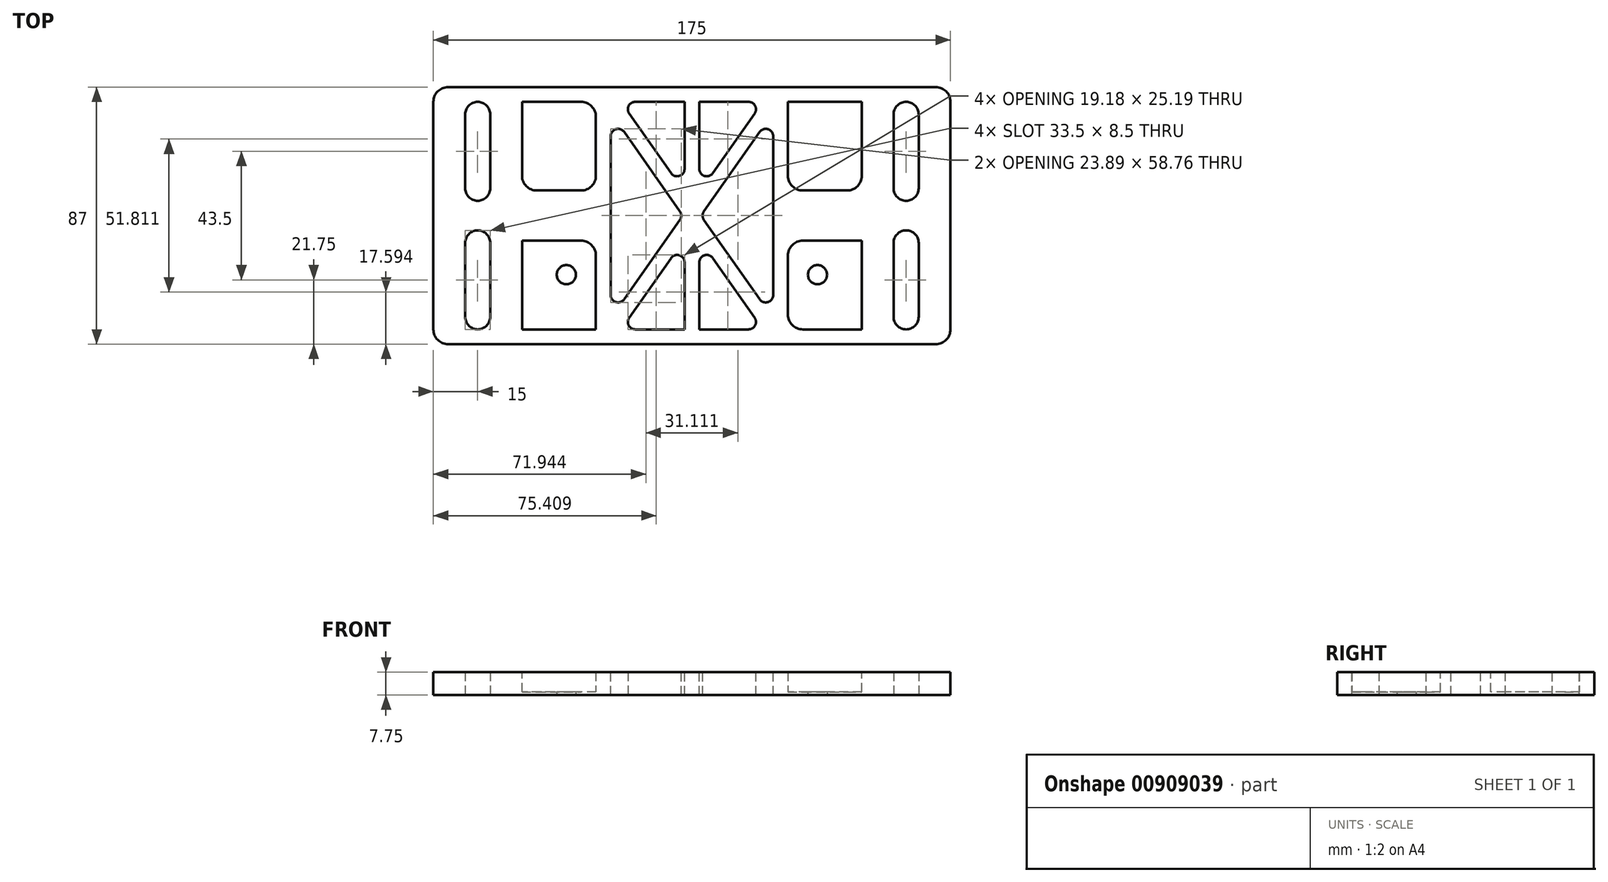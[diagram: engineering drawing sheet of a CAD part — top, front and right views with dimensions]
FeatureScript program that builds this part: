
annotation { "Feature Type Name" : "Feature", "Feature Type Description" : "" }
export const myFeature = defineFeature(function(context is Context, id is Id, definition is map)
    precondition{}
    {
        {
            var Q0;
            Q0=qCreatedBy(makeId("Top.planeOp"),FACE);
            var sketch = newSketch(context, id + "F0", { "sketchPlane" : qUnion([Q0])});
            skLineSegment(sketch, "E0.bottom", {"start": v(-52.5, 43.5) * mm, "end": v(52.5, 43.5) * mm});
            skLineSegment(sketch, "E0.top", {"start": v(-52.5, -43.5) * mm, "end": v(52.5, -43.5) * mm});
            skLineSegment(sketch, "E0.left", {"start": v(-52.5, 43.5) * mm, "end": v(-52.5, -43.5) * mm});
            skLineSegment(sketch, "E0.right", {"start": v(52.5, 43.5) * mm, "end": v(52.5, -43.5) * mm});
            skPoint(sketch, "E0.middle", {"position": v(0, 0) * mm});
            skSolve(sketch);
        }
        {
            var Q0;
            Q0=makeQuery(id+"F2.imprint","IMPRINT",FACE,{"disambiguationData":[TD([[makeQuery(id+"F2.imprint","IMPRINT",EDGE,{"derivedFrom":sQuery(id+"F2.wireOp",EDGE,"E1")}),-1.0]])]});
            var Q1;
            Q1=makeQuery(id+"F2.imprint","IMPRINT",FACE,{"disambiguationData":[TD([[makeQuery(id+"F2.imprint","IMPRINT",EDGE,{"derivedFrom":sQuery(id+"F2.wireOp",EDGE,"E1")}),1.0]])]});
            var Q2;
            Q2=makeQuery(id+"F0.imprint","IMPRINT",FACE,{"disambiguationData":[TD([[makeQuery(id+"F0.imprint","IMPRINT",EDGE,{"derivedFrom":sQuery(id+"F0.wireOp",EDGE,"E0.bottom")}),-1.0]])]});
            extrude(context, id + "F1", {"entities" : qUnion([Q0, Q1, Q2]), "depth" : 1 * mm, "offsetDistance" : 25 * mm});
        }
        {
            var Q0;
            Q0=makeQuery(id+"F0.imprint","IMPRINT",FACE,{"disambiguationData":[TD([[makeQuery(id+"F0.imprint","IMPRINT",EDGE,{"derivedFrom":sQuery(id+"F0.wireOp",EDGE,"E0.bottom")}),-1.0]])]});
            var sketch = newSketch(context, id + "F2", { "sketchPlane" : qUnion([Q0])});
            skCircle(sketch, "E1", {"center": v(-42.5, -20) * mm, "radius": 3.25 * mm});
            skCircle(sketch, "E2", {"center": v(42.5, -20) * mm, "radius": 3.25 * mm});
            skSolve(sketch);
        }
        {
            var Q0;
            Q0=makeQuery(id+"F2.imprint","IMPRINT",FACE,{"disambiguationData":[TD([[makeQuery(id+"F2.imprint","IMPRINT",EDGE,{"derivedFrom":sQuery(id+"F2.wireOp",EDGE,"E1")}),1.0]])]});
            var Q1;
            Q1=makeQuery(id+"F2.imprint","IMPRINT",FACE,{"disambiguationData":[TD([[makeQuery(id+"F2.imprint","IMPRINT",EDGE,{"derivedFrom":sQuery(id+"F2.wireOp",EDGE,"E2")}),1.0]])]});
            var Q2;
            Q2=makeQuery(id+"FSkjlowhmZpUpf8_1.1.F2.imprint","IMPRINT",FACE,{"disambiguationData":[TD([[makeQuery(id+"FSkjlowhmZpUpf8_1.1.F2.imprint","IMPRINT",EDGE,{"derivedFrom":sQuery(id+"FSkjlowhmZpUpf8_1.1.F2.wireOp",EDGE,"E2")}),1.0]])]});
            var Q3;
            Q3=makeQuery(id+"FSkjlowhmZpUpf8_1.1.F2.imprint","IMPRINT",FACE,{"disambiguationData":[TD([[makeQuery(id+"FSkjlowhmZpUpf8_1.1.F2.imprint","IMPRINT",EDGE,{"derivedFrom":sQuery(id+"FSkjlowhmZpUpf8_1.1.F2.wireOp",EDGE,"E1")}),1.0]])]});
            extrude(context, id + "F3", {"entities" : qUnion([Q0, Q1, Q2, Q3]), "operationType" : NewBodyOperationType.REMOVE, "endBound" : BoundingType.THROUGH_ALL, "depth" : 25 * mm, "offsetDistance" : 25 * mm});
        }
        {
            var Q0;
            Q0=makeQuery(id+"F1.opExtrude","CAP_FACE",FACE,{"disambiguationData":[OSD([sQuery(id+"F0.wireOp",EDGE,"E0.bottom"),sQuery(id+"F0.wireOp",EDGE,"E0.top"),sQuery(id+"F0.wireOp",EDGE,"E0.left"),sQuery(id+"F0.wireOp",EDGE,"E0.right")])],"isStart":false});
            var sketch = newSketch(context, id + "F4", { "sketchPlane" : qUnion([Q0])});
            skLineSegment(sketch, "E3.bottom", {"start": v(-52.5, 43.5) * mm, "end": v(-32.5, 43.5) * mm});
            skLineSegment(sketch, "E3.top", {"start": v(-52.5, 8.5) * mm, "end": v(-32.5, 8.5) * mm});
            skLineSegment(sketch, "E3.left", {"start": v(-52.5, 43.5) * mm, "end": v(-52.5, 8.5) * mm});
            skLineSegment(sketch, "E3.right", {"start": v(-32.5, 43.5) * mm, "end": v(-32.5, 8.5) * mm});
            skLineSegment(sketch, "E4.1.0.0", {"start": v(32.5, 43.5) * mm, "end": v(52.5, 43.5) * mm});
            skLineSegment(sketch, "E4.1.0.1", {"start": v(52.5, 43.5) * mm, "end": v(52.5, 8.5) * mm});
            skLineSegment(sketch, "E4.1.0.2", {"start": v(32.5, 8.5) * mm, "end": v(52.5, 8.5) * mm});
            skLineSegment(sketch, "E4.direction1", {"start": v(-52.5, 43.5) * mm, "end": v(32.5, 43.5) * mm, "construction": true});
            skLineSegment(sketch, "E5.MirrorCS", {"start": v(-52.5, -8.5) * mm, "end": v(-32.5, -8.5) * mm});
            skLineSegment(sketch, "E6.MirrorCS", {"start": v(-52.5, -43.5) * mm, "end": v(-52.5, -8.5) * mm});
            skLineSegment(sketch, "E7.MirrorCS", {"start": v(-52.5, -43.5) * mm, "end": v(32.5, -43.5) * mm, "construction": true});
            skLineSegment(sketch, "E8.MirrorCS", {"start": v(-32.5, -43.5) * mm, "end": v(-32.5, -8.5) * mm});
            skLineSegment(sketch, "E9.MirrorCS", {"start": v(32.5, -8.5) * mm, "end": v(52.5, -8.5) * mm});
            skLineSegment(sketch, "E10.MirrorCS", {"start": v(52.5, -43.5) * mm, "end": v(52.5, -8.5) * mm});
            skLineSegment(sketch, "E11.MirrorCS", {"start": v(32.5, -43.5) * mm, "end": v(52.5, -43.5) * mm});
            skLineSegment(sketch, "E12", {"start": v(32.5, 43.5) * mm, "end": v(32.5, 8.5) * mm});
            skLineSegment(sketch, "E13", {"start": v(32.5, -8.5) * mm, "end": v(32.5, -43.5) * mm});
            skSolve(sketch);
        }
        {
            var Q0;
            {var subQ0=sQuery(id+"F4.wireOp",EDGE,"E3.top");Q0=makeQuery(id+"F4.imprint","IMPRINT",FACE,{"disambiguationData":[TD([[makeQuery(id+"F4.imprint","IMPRINT",EDGE,{"derivedFrom":subQ0}),-1.0]])]});}
            extrude(context, id + "F5", {"entities" : qUnion([Q0]), "operationType" : NewBodyOperationType.ADD, "depth" : (1 + 4.25 + 1.5) * mm, "offsetDistance" : 25 * mm});
        }
        {
            var Q0;
            Q0=makeQuery(id+"F5.opExtrude","CAP_FACE",FACE,{"disambiguationData":[OSD([sQuery(id+"F0.wireOp",EDGE,"E0.bottom"),sQuery(id+"F0.wireOp",EDGE,"E0.top"),sQuery(id+"F0.wireOp",EDGE,"E0.left"),sQuery(id+"F0.wireOp",EDGE,"E0.right"),sQuery(id+"F4.wireOp",EDGE,"E3.top"),sQuery(id+"F4.wireOp",EDGE,"E3.right"),sQuery(id+"F4.wireOp",EDGE,"E4.1.0.2"),sQuery(id+"F4.wireOp",EDGE,"E5.MirrorCS"),sQuery(id+"F4.wireOp",EDGE,"E8.MirrorCS"),sQuery(id+"F4.wireOp",EDGE,"E9.MirrorCS"),sQuery(id+"F4.wireOp",EDGE,"E12"),sQuery(id+"F4.wireOp",EDGE,"E13")])],"isStart":false});
            var sketch = newSketch(context, id + "F6", { "sketchPlane" : qUnion([Q0])});
            skLineSegment(sketch, "E14.0", {"start": v(-27.5, -38.5) * mm, "end": v(27.5, -38.5) * mm});
            skLineSegment(sketch, "E14.5", {"start": v(27.5, 38.5) * mm, "end": v(-27.5, 38.5) * mm});
            skLineSegment(sketch, "E15.bottom", {"start": v(-2.5, 38.5) * mm, "end": v(2.5, 38.5) * mm});
            skLineSegment(sketch, "E15.top", {"start": v(-2.5, -38.5) * mm, "end": v(2.5, -38.5) * mm});
            skLineSegment(sketch, "E15.left", {"start": v(-2.5, 38.5) * mm, "end": v(-2.5, -38.5) * mm});
            skLineSegment(sketch, "E15.right", {"start": v(2.5, 38.5) * mm, "end": v(2.5, -38.5) * mm});
            skLineSegment(sketch, "E16", {"start": v(-27.5, 38.5) * mm, "end": v(-27.5, -38.5) * mm});
            skLineSegment(sketch, "E17", {"start": v(27.5, -38.5) * mm, "end": v(27.5, 38.5) * mm});
            skLineSegment(sketch, "E18", {"start": v(-27.5, 34.78) * mm, "end": v(24, -38.5) * mm});
            skLineSegment(sketch, "E19", {"start": v(-24, 38.5) * mm, "end": v(27.5, -34.78) * mm});
            skLineSegment(sketch, "E20", {"start": v(24, -38.5) * mm, "end": v(27.5, -38.5) * mm});
            skLineSegment(sketch, "E21", {"start": v(27.5, -34.78) * mm, "end": v(27.5, -38.5) * mm});
            skLineSegment(sketch, "E22.MirrorCS", {"start": v(-27.5, -34.78) * mm, "end": v(24, 38.5) * mm});
            skLineSegment(sketch, "E23.MirrorCS", {"start": v(-24, -38.5) * mm, "end": v(27.5, 34.78) * mm});
            skSolve(sketch);
        }
        {
            var Q0;
            {var subQ0=sQuery(id+"F6.wireOp",EDGE,"E18");var subQ1=sQuery(id+"F6.wireOp",EDGE,"E16");var subQ2=makeQuery(id+"F6.imprint","INTERSECT",VERTEX,{"derivedFrom":[subQ1,subQ0]});Q0=makeQuery(id+"F6.imprint","IMPRINT",FACE,{"disambiguationData":[TD([[makeQuery(id+"F6.imprint","IMPRINT",EDGE,{"disambiguationData":[TD([[subQ2,-1.0]])],"derivedFrom":subQ1}),1.0]])]});}
            var Q1;
            {var subQ1=sQuery(id+"F6.wireOp",EDGE,"E14.5");var subQ3=sQuery(id+"F6.wireOp",EDGE,"E19");var subQ4=makeQuery(id+"F6.imprint","INTERSECT",VERTEX,{"derivedFrom":[subQ1,subQ3]});Q1=makeQuery(id+"F6.imprint","IMPRINT",FACE,{"disambiguationData":[TD([[makeQuery(id+"F6.imprint","IMPRINT",EDGE,{"disambiguationData":[TD([[subQ4,-1.0]])],"derivedFrom":subQ3}),1.0]])]});}
            var Q2;
            {var subQ6=sQuery(id+"F6.wireOp",EDGE,"E15.bottom");Q2=makeQuery(id+"F6.imprint","IMPRINT",FACE,{"disambiguationData":[TD([[makeQuery(id+"F6.imprint","IMPRINT",EDGE,{"derivedFrom":subQ6}),-1.0]])]});}
            var Q3;
            {var subQ1=sQuery(id+"F6.wireOp",EDGE,"E14.5");var subQ3=sQuery(id+"F6.wireOp",EDGE,"E22.MirrorCS");var subQ4=makeQuery(id+"F6.imprint","INTERSECT",VERTEX,{"derivedFrom":[subQ1,subQ3]});Q3=makeQuery(id+"F6.imprint","IMPRINT",FACE,{"disambiguationData":[TD([[makeQuery(id+"F6.imprint","IMPRINT",EDGE,{"disambiguationData":[TD([[subQ4,1.0]])],"derivedFrom":subQ3}),1.0]])]});}
            var Q4;
            {var subQ1=sQuery(id+"F6.wireOp",EDGE,"E17");var subQ3=sQuery(id+"F6.wireOp",EDGE,"E23.MirrorCS");var subQ4=makeQuery(id+"F6.imprint","INTERSECT",VERTEX,{"derivedFrom":[subQ1,subQ3]});Q4=makeQuery(id+"F6.imprint","IMPRINT",FACE,{"disambiguationData":[TD([[makeQuery(id+"F6.imprint","IMPRINT",EDGE,{"disambiguationData":[TD([[subQ4,1.0]])],"derivedFrom":subQ3}),-1.0]])]});}
            var Q5;
            {var subQ0=sQuery(id+"F6.wireOp",EDGE,"E18");var subQ3=sQuery(id+"F6.wireOp",EDGE,"E15.right");var subQ5=makeQuery(id+"F6.imprint","INTERSECT",VERTEX,{"derivedFrom":[subQ3,subQ0]});Q5=makeQuery(id+"F6.imprint","IMPRINT",FACE,{"disambiguationData":[TD([[makeQuery(id+"F6.imprint","IMPRINT",EDGE,{"disambiguationData":[TD([[subQ5,-1.0]])],"derivedFrom":subQ3}),1.0]])]});}
            var Q6;
            {var subQ5=sQuery(id+"F6.wireOp",EDGE,"E15.top");Q6=makeQuery(id+"F6.imprint","IMPRINT",FACE,{"disambiguationData":[TD([[makeQuery(id+"F6.imprint","IMPRINT",EDGE,{"derivedFrom":subQ5}),1.0]])]});}
            var Q7;
            {var subQ1=sQuery(id+"F6.wireOp",EDGE,"E14.0");var subQ3=sQuery(id+"F6.wireOp",EDGE,"E23.MirrorCS");var subQ4=makeQuery(id+"F6.imprint","INTERSECT",VERTEX,{"derivedFrom":[subQ1,subQ3]});Q7=makeQuery(id+"F6.imprint","IMPRINT",FACE,{"disambiguationData":[TD([[makeQuery(id+"F6.imprint","IMPRINT",EDGE,{"disambiguationData":[TD([[subQ4,-1.0]])],"derivedFrom":subQ3}),-1.0]])]});}
            extrude(context, id + "F7", {"entities" : qUnion([Q0, Q1, Q2, Q3, Q4, Q5, Q6, Q7]), "operationType" : NewBodyOperationType.REMOVE, "oppositeDirection" : true, "depth" : 25 * mm, "offsetDistance" : 25 * mm});
        }
        {
            var Q0;
            Q0=makeQuery(id+"F0.imprint","IMPRINT",FACE,{"disambiguationData":[TD([[makeQuery(id+"F0.imprint","IMPRINT",EDGE,{"derivedFrom":sQuery(id+"F0.wireOp",EDGE,"E0.bottom")}),-1.0]])]});
            var sketch = newSketch(context, id + "F8", { "sketchPlane" : qUnion([Q0])});
            skLineSegment(sketch, "E24.bottom", {"start": v(87.5, 43.5) * mm, "end": v(57.5, 43.5) * mm});
            skLineSegment(sketch, "E24.top", {"start": v(87.5, -43.5) * mm, "end": v(57.5, -43.5) * mm});
            skLineSegment(sketch, "E24.left", {"start": v(87.5, 43.5) * mm, "end": v(87.5, -43.5) * mm});
            skLineSegment(sketch, "E24.right", {"start": v(-87.5, 43.5) * mm, "end": v(-87.5, -43.5) * mm});
            skPoint(sketch, "E24.middle", {"position": v(0, 0) * mm});
            skLineSegment(sketch, "E25", {"start": v(57.5, -43.5) * mm, "end": v(57.5, 43.5) * mm});
            skLineSegment(sketch, "E26", {"start": v(-57.5, -43.5) * mm, "end": v(-57.5, 43.5) * mm});
            skLineSegment(sketch, "E27.trimOffspring", {"start": v(-57.5, -43.5) * mm, "end": v(-87.5, -43.5) * mm});
            skLineSegment(sketch, "E28.trimOffspring", {"start": v(-57.5, 43.5) * mm, "end": v(-87.5, 43.5) * mm});
            skLineSegment(sketch, "E29.bottom", {"start": v(57.5, -43.5) * mm, "end": v(52.5, -43.5) * mm});
            skLineSegment(sketch, "E29.top", {"start": v(57.5, 43.5) * mm, "end": v(52.5, 43.5) * mm});
            skLineSegment(sketch, "E29.right", {"start": v(52.5, -43.5) * mm, "end": v(52.5, 43.5) * mm});
            skLineSegment(sketch, "E30.bottom", {"start": v(-57.5, -43.5) * mm, "end": v(-52.5, -43.5) * mm});
            skLineSegment(sketch, "E30.top", {"start": v(-57.5, 43.5) * mm, "end": v(-52.5, 43.5) * mm});
            skLineSegment(sketch, "E30.right", {"start": v(-52.5, -43.5) * mm, "end": v(-52.5, 43.5) * mm});
            skSolve(sketch);
        }
        {
            var Q0;
            {var subQ3=sQuery(id+"F8.wireOp",EDGE,"E24.bottom");Q0=makeQuery(id+"F8.imprint","IMPRINT",FACE,{"disambiguationData":[TD([[makeQuery(id+"F8.imprint","IMPRINT",EDGE,{"derivedFrom":subQ3}),1.0]])]});}
            var Q1;
            Q1=makeQuery(id+"F8.imprint","IMPRINT",FACE,{"disambiguationData":[TD([[makeQuery(id+"F8.imprint","IMPRINT",EDGE,{"derivedFrom":sQuery(id+"F8.wireOp",EDGE,"E29.bottom")}),-1.0]])]});
            var Q2;
            Q2=makeQuery(id+"F8.imprint","IMPRINT",FACE,{"disambiguationData":[TD([[makeQuery(id+"F8.imprint","IMPRINT",EDGE,{"derivedFrom":sQuery(id+"F8.wireOp",EDGE,"E30.bottom")}),1.0]])]});
            var Q3;
            Q3=makeQuery(id+"F8.imprint","IMPRINT",FACE,{"disambiguationData":[TD([[makeQuery(id+"F8.imprint","IMPRINT",EDGE,{"derivedFrom":sQuery(id+"F8.wireOp",EDGE,"E24.right")}),1.0]])]});
            var Q4;
            {var subQ0=sQuery(id+"F0.wireOp",EDGE,"E0.top");var subQ1=sQuery(id+"F0.wireOp",EDGE,"E0.left");Q4=makeQuery(id+"F5.boolean.opBoolean","SPLIT",FACE,{"disambiguationData":[TD([makeQuery(id+"F5.opExtrude","SWEPT_FACE",FACE,{"disambiguationData":[OSD([sQuery(id+"F4.wireOp",EDGE,"E5.MirrorCS")])]})])],"derivedFrom":makeQuery(id+"F1.opExtrude","CAP_FACE",FACE,{"disambiguationData":[OSD([sQuery(id+"F0.wireOp",EDGE,"E0.bottom"),subQ0,subQ1,sQuery(id+"F0.wireOp",EDGE,"E0.right")])],"isStart":false})});}
            extrude(context, id + "F9", {"entities" : qUnion([Q0, Q1, Q2, Q3]), "operationType" : NewBodyOperationType.ADD, "endBound" : BoundingType.UP_TO_SURFACE, "depth" : 25 * mm, "endBoundEntityFace" : qUnion([Q4]), "offsetDistance" : 25 * mm});
        }
        {
            var Q0;
            Q0=makeQuery(id+"F5.opExtrude","SWEPT_EDGE",EDGE,{"disambiguationData":[OSD([sQuery(id+"F4.wireOp",EDGE,"E4.1.0.2"),sQuery(id+"F4.wireOp",EDGE,"E12")])]});
            var Q1;
            Q1=makeQuery(id+"F5.opExtrude","SWEPT_EDGE",EDGE,{"disambiguationData":[OSD([sQuery(id+"F0.wireOp",EDGE,"E0.bottom"),sQuery(id+"F4.wireOp",EDGE,"E4.1.0.0"),sQuery(id+"F4.wireOp",EDGE,"E12")])]});
            var Q2;
            Q2=makeQuery(id+"F5.opExtrude","SWEPT_EDGE",EDGE,{"disambiguationData":[OSD([sQuery(id+"F0.wireOp",EDGE,"E0.bottom"),sQuery(id+"F4.wireOp",EDGE,"E3.bottom"),sQuery(id+"F4.wireOp",EDGE,"E3.right")])]});
            var Q3;
            Q3=makeQuery(id+"F5.opExtrude","SWEPT_EDGE",EDGE,{"disambiguationData":[OSD([sQuery(id+"F4.wireOp",EDGE,"E3.top"),sQuery(id+"F4.wireOp",EDGE,"E3.right")])]});
            var Q4;
            Q4=makeQuery(id+"F5.opExtrude","SWEPT_EDGE",EDGE,{"disambiguationData":[OSD([sQuery(id+"F4.wireOp",EDGE,"E5.MirrorCS"),sQuery(id+"F4.wireOp",EDGE,"E8.MirrorCS")])]});
            var Q5;
            Q5=makeQuery(id+"F5.opExtrude","SWEPT_EDGE",EDGE,{"disambiguationData":[OSD([sQuery(id+"F0.wireOp",EDGE,"E0.top"),sQuery(id+"F4.wireOp",EDGE,"E8.MirrorCS")])]});
            var Q6;
            Q6=makeQuery(id+"F5.opExtrude","SWEPT_EDGE",EDGE,{"disambiguationData":[OSD([sQuery(id+"F0.wireOp",EDGE,"E0.top"),sQuery(id+"F4.wireOp",EDGE,"E11.MirrorCS"),sQuery(id+"F4.wireOp",EDGE,"E13")])]});
            var Q7;
            Q7=makeQuery(id+"F5.opExtrude","SWEPT_EDGE",EDGE,{"disambiguationData":[OSD([sQuery(id+"F4.wireOp",EDGE,"E9.MirrorCS"),sQuery(id+"F4.wireOp",EDGE,"E13")])]});
            var Q8;
            Q8=makeQuery(id+"F5.opExtrude","SWEPT_EDGE",EDGE,{"disambiguationData":[OSD([sQuery(id+"F0.wireOp",EDGE,"E0.left"),sQuery(id+"F4.wireOp",EDGE,"E3.top"),sQuery(id+"F4.wireOp",EDGE,"E3.left")])]});
            var Q9;
            Q9=makeQuery(id+"F9.opExtrude","SWEPT_EDGE",EDGE,{"disambiguationData":[OSD([sQuery(id+"F0.wireOp",EDGE,"E0.left"),sQuery(id+"F8.wireOp",EDGE,"E24.bottom")])]});
            var Q10;
            Q10=makeQuery(id+"F9.opExtrude","SWEPT_EDGE",EDGE,{"disambiguationData":[OSD([sQuery(id+"F0.wireOp",EDGE,"E0.left"),sQuery(id+"F8.wireOp",EDGE,"E24.top")])]});
            var Q11;
            Q11=makeQuery(id+"F5.opExtrude","SWEPT_EDGE",EDGE,{"disambiguationData":[OSD([sQuery(id+"F0.wireOp",EDGE,"E0.left"),sQuery(id+"F4.wireOp",EDGE,"E5.MirrorCS"),sQuery(id+"F4.wireOp",EDGE,"E6.MirrorCS")])]});
            var Q12;
            Q12=makeQuery(id+"F9.opExtrude","SWEPT_EDGE",EDGE,{"disambiguationData":[OSD([sQuery(id+"F8.wireOp",EDGE,"E24.top"),sQuery(id+"F8.wireOp",EDGE,"E24.right")])]});
            var Q13;
            Q13=makeQuery(id+"F9.opExtrude","SWEPT_EDGE",EDGE,{"disambiguationData":[OSD([sQuery(id+"F8.wireOp",EDGE,"E24.bottom"),sQuery(id+"F8.wireOp",EDGE,"E24.right")])]});
            var Q14;
            Q14=makeQuery(id+"F9.opExtrude","SWEPT_EDGE",EDGE,{"disambiguationData":[OSD([sQuery(id+"F8.wireOp",EDGE,"E24.bottom"),sQuery(id+"F8.wireOp",EDGE,"E24.left")])]});
            var Q15;
            Q15=makeQuery(id+"F9.opExtrude","SWEPT_EDGE",EDGE,{"disambiguationData":[OSD([sQuery(id+"F8.wireOp",EDGE,"E24.top"),sQuery(id+"F8.wireOp",EDGE,"E24.left")])]});
            var Q16;
            Q16=makeQuery(id+"F9.opExtrude","SWEPT_EDGE",EDGE,{"disambiguationData":[OSD([sQuery(id+"F0.wireOp",EDGE,"E0.right"),sQuery(id+"F8.wireOp",EDGE,"E24.bottom")])]});
            var Q17;
            Q17=makeQuery(id+"F5.opExtrude","SWEPT_EDGE",EDGE,{"disambiguationData":[OSD([sQuery(id+"F0.wireOp",EDGE,"E0.right"),sQuery(id+"F4.wireOp",EDGE,"E4.1.0.1"),sQuery(id+"F4.wireOp",EDGE,"E4.1.0.2")])]});
            var Q18;
            Q18=makeQuery(id+"F9.opExtrude","SWEPT_EDGE",EDGE,{"disambiguationData":[OSD([sQuery(id+"F0.wireOp",EDGE,"E0.right"),sQuery(id+"F8.wireOp",EDGE,"E24.top")])]});
            var Q19;
            Q19=makeQuery(id+"F5.opExtrude","SWEPT_EDGE",EDGE,{"disambiguationData":[OSD([sQuery(id+"F0.wireOp",EDGE,"E0.right"),sQuery(id+"F4.wireOp",EDGE,"E9.MirrorCS"),sQuery(id+"F4.wireOp",EDGE,"E10.MirrorCS")])]});
            fillet(context, id + "F10", {"entities" : qUnion([Q0, Q1, Q2, Q3, Q4, Q5, Q6, Q7, Q8, Q9, Q10, Q11, Q12, Q13, Q14, Q15, Q16, Q17, Q18, Q19]), "radius" : 5 * mm, "tangentPropagation" : true, "allowEdgeOverflow" : false});
        }
        {
            var Q0;
            {var subQ0=sQuery(id+"F8.wireOp",EDGE,"E24.left");Q0=makeQuery(id+"F8.imprint","IMPRINT",FACE,{"disambiguationData":[TD([[makeQuery(id+"F8.imprint","IMPRINT",EDGE,{"derivedFrom":subQ0}),-1.0]])]});}
            var Q1;
            {var subQ0=sQuery(id+"F8.wireOp",EDGE,"E24.right");Q1=makeQuery(id+"F8.imprint","IMPRINT",FACE,{"disambiguationData":[TD([[makeQuery(id+"F8.imprint","IMPRINT",EDGE,{"derivedFrom":subQ0}),1.0]])]});}
            var Q2;
            Q2=makeQuery(id+"F5.opExtrude","CAP_FACE",FACE,{"disambiguationData":[OSD([sQuery(id+"F0.wireOp",EDGE,"E0.bottom"),sQuery(id+"F0.wireOp",EDGE,"E0.top"),sQuery(id+"F0.wireOp",EDGE,"E0.left"),sQuery(id+"F0.wireOp",EDGE,"E0.right"),sQuery(id+"F4.wireOp",EDGE,"E3.top"),sQuery(id+"F4.wireOp",EDGE,"E3.right"),sQuery(id+"F4.wireOp",EDGE,"E4.1.0.2"),sQuery(id+"F4.wireOp",EDGE,"E5.MirrorCS"),sQuery(id+"F4.wireOp",EDGE,"E8.MirrorCS"),sQuery(id+"F4.wireOp",EDGE,"E9.MirrorCS"),sQuery(id+"F4.wireOp",EDGE,"E12"),sQuery(id+"F4.wireOp",EDGE,"E13")])],"isStart":false});
            extrude(context, id + "F11", {"entities" : qUnion([Q0, Q1]), "operationType" : NewBodyOperationType.ADD, "endBound" : BoundingType.UP_TO_SURFACE, "depth" : 25 * mm, "endBoundEntityFace" : qUnion([Q2]), "offsetDistance" : 25 * mm});
        }
        {
            var Q0;
            Q0=makeQuery(id+"F5.opExtrude","CAP_FACE",FACE,{"disambiguationData":[OSD([sQuery(id+"F0.wireOp",EDGE,"E0.bottom"),sQuery(id+"F0.wireOp",EDGE,"E0.top"),sQuery(id+"F0.wireOp",EDGE,"E0.left"),sQuery(id+"F0.wireOp",EDGE,"E0.right"),sQuery(id+"F4.wireOp",EDGE,"E3.top"),sQuery(id+"F4.wireOp",EDGE,"E3.right"),sQuery(id+"F4.wireOp",EDGE,"E4.1.0.2"),sQuery(id+"F4.wireOp",EDGE,"E5.MirrorCS"),sQuery(id+"F4.wireOp",EDGE,"E8.MirrorCS"),sQuery(id+"F4.wireOp",EDGE,"E9.MirrorCS"),sQuery(id+"F4.wireOp",EDGE,"E12"),sQuery(id+"F4.wireOp",EDGE,"E13")])],"isStart":false});
            var sketch = newSketch(context, id + "F12", { "sketchPlane" : qUnion([Q0])});
            skLineSegment(sketch, "E31.bottom", {"start": v(47.5, -8.5) * mm, "end": v(57.5, -8.5) * mm});
            skLineSegment(sketch, "E31.top", {"start": v(47.5, 8.5) * mm, "end": v(57.5, 8.5) * mm});
            skLineSegment(sketch, "E31.left", {"start": v(47.5, -8.5) * mm, "end": v(47.5, 8.5) * mm});
            skLineSegment(sketch, "E31.right", {"start": v(57.5, -8.5) * mm, "end": v(57.5, 8.5) * mm});
            skLineSegment(sketch, "E32.bottom", {"start": v(-47.5, -8.5) * mm, "end": v(-57.5, -8.5) * mm});
            skLineSegment(sketch, "E32.top", {"start": v(-47.5, 8.5) * mm, "end": v(-57.5, 8.5) * mm});
            skLineSegment(sketch, "E32.left", {"start": v(-47.5, -8.5) * mm, "end": v(-47.5, 8.5) * mm});
            skLineSegment(sketch, "E32.right", {"start": v(-57.5, -8.5) * mm, "end": v(-57.5, 8.5) * mm});
            skSolve(sketch);
        }
        {
            var Q0;
            Q0=makeQuery(id+"F12.imprint","IMPRINT",FACE,{"disambiguationData":[TD([[makeQuery(id+"F12.imprint","IMPRINT",EDGE,{"derivedFrom":sQuery(id+"F12.wireOp",EDGE,"E31.bottom")}),1.0]])]});
            var Q1;
            Q1=makeQuery(id+"F12.imprint","IMPRINT",FACE,{"disambiguationData":[TD([[makeQuery(id+"F12.imprint","IMPRINT",EDGE,{"derivedFrom":sQuery(id+"F12.wireOp",EDGE,"E32.bottom")}),-1.0]])]});
            var Q2;
            {var subQ0=sQuery(id+"F0.wireOp",EDGE,"E0.right");var subQ2=sQuery(id+"F0.wireOp",EDGE,"E0.bottom");var subQ4=sQuery(id+"F0.wireOp",EDGE,"E0.top");var subQ5=makeQuery(id+"F1.opExtrude","CAP_FACE",FACE,{"disambiguationData":[OSD([subQ2,subQ4,sQuery(id+"F0.wireOp",EDGE,"E0.left"),subQ0])],"isStart":false});Q2=makeQuery(id+"F9.boolean.opBoolean","MERGE",FACE,{"derivedFrom":[makeQuery(id+"F5.boolean.opBoolean","SPLIT",FACE,{"disambiguationData":[TD([makeQuery(id+"F3.boolean.opBoolean","COPY",FACE,{"derivedFrom":makeQuery(id+"F3.opExtrude","SWEPT_FACE",FACE,{"disambiguationData":[OSD([sQuery(id+"F2.wireOp",EDGE,"E2")])]})})])],"derivedFrom":subQ5}),makeQuery(id+"F5.boolean.opBoolean","SPLIT",FACE,{"disambiguationData":[TD([makeQuery(id+"F3.boolean.opBoolean","COPY",FACE,{"derivedFrom":makeQuery(id+"F3.opExtrude","SWEPT_FACE",FACE,{"disambiguationData":[OSD([sQuery(id+"FSkjlowhmZpUpf8_1.1.F2.wireOp",EDGE,"E2")])]})})])],"derivedFrom":subQ5}),makeQuery(id+"F9.opExtrude","CAP_FACE",FACE,{"disambiguationData":[OSD([subQ0,sQuery(id+"F8.wireOp",EDGE,"E24.bottom"),sQuery(id+"F8.wireOp",EDGE,"E24.top"),sQuery(id+"F8.wireOp",EDGE,"E24.left")])],"isStart":false})]});}
            extrude(context, id + "F13", {"entities" : qUnion([Q0, Q1, Q2]), "operationType" : NewBodyOperationType.ADD, "endBound" : BoundingType.UP_TO_NEXT, "oppositeDirection" : true, "depth" : 25 * mm, "offsetDistance" : 25 * mm});
        }
        {
            var Q0;
            {var subQ0=sQuery(id+"F8.wireOp",EDGE,"E24.top");var subQ1=sQuery(id+"F8.wireOp",EDGE,"E24.bottom");var subQ2=sQuery(id+"F0.wireOp",EDGE,"E0.left");var subQ3=sQuery(id+"F0.wireOp",EDGE,"E0.right");Q0=makeQuery(id+"F9.boolean.opBoolean","MERGE",FACE,{"derivedFrom":[makeQuery(id+"F5.opExtrude","CAP_FACE",FACE,{"disambiguationData":[OSD([sQuery(id+"F0.wireOp",EDGE,"E0.bottom"),sQuery(id+"F0.wireOp",EDGE,"E0.top"),subQ2,subQ3,sQuery(id+"F4.wireOp",EDGE,"E3.top"),sQuery(id+"F4.wireOp",EDGE,"E3.right"),sQuery(id+"F4.wireOp",EDGE,"E4.1.0.2"),sQuery(id+"F4.wireOp",EDGE,"E5.MirrorCS"),sQuery(id+"F4.wireOp",EDGE,"E8.MirrorCS"),sQuery(id+"F4.wireOp",EDGE,"E9.MirrorCS"),sQuery(id+"F4.wireOp",EDGE,"E12"),sQuery(id+"F4.wireOp",EDGE,"E13")])],"isStart":false}),makeQuery(id+"F9.opExtrude","CAP_FACE",FACE,{"disambiguationData":[OSD([subQ3,subQ1,subQ0,sQuery(id+"F8.wireOp",EDGE,"E24.left")])],"isStart":false}),makeQuery(id+"F9.opExtrude","CAP_FACE",FACE,{"disambiguationData":[OSD([subQ2,subQ1,subQ0,sQuery(id+"F8.wireOp",EDGE,"E24.right")])],"isStart":false})]});}
            var sketch = newSketch(context, id + "F14", { "sketchPlane" : qUnion([Q0])});
            skLineSegment(sketch, "E33.bottom", {"start": v(76.75, -38.5) * mm, "end": v(68.25, -38.5) * mm});
            skLineSegment(sketch, "E33.top", {"start": v(76.75, 38.5) * mm, "end": v(68.25, 38.5) * mm});
            skLineSegment(sketch, "E33.left", {"start": v(76.75, -38.5) * mm, "end": v(76.75, 38.5) * mm});
            skLineSegment(sketch, "E33.right", {"start": v(68.25, -38.5) * mm, "end": v(68.25, 38.5) * mm});
            skLineSegment(sketch, "E34.MirrorCS", {"start": v(-76.75, -38.5) * mm, "end": v(-76.75, 38.5) * mm});
            skLineSegment(sketch, "E35.MirrorCS", {"start": v(-76.75, -38.5) * mm, "end": v(-68.25, -38.5) * mm});
            skLineSegment(sketch, "E36.MirrorCS", {"start": v(-68.25, -38.5) * mm, "end": v(-68.25, 38.5) * mm});
            skLineSegment(sketch, "E37.MirrorCS", {"start": v(-76.75, 38.5) * mm, "end": v(-68.25, 38.5) * mm});
            skLineSegment(sketch, "E38.bottom", {"start": v(76.75, -5) * mm, "end": v(68.25, -5) * mm});
            skLineSegment(sketch, "E38.top", {"start": v(76.75, 5) * mm, "end": v(68.25, 5) * mm});
            skLineSegment(sketch, "E38.left", {"start": v(76.75, -5) * mm, "end": v(76.75, 5) * mm});
            skLineSegment(sketch, "E38.right", {"start": v(68.25, -5) * mm, "end": v(68.25, 5) * mm});
            skLineSegment(sketch, "E39.MirrorCS", {"start": v(-76.75, -5) * mm, "end": v(-68.25, -5) * mm});
            skLineSegment(sketch, "E40.MirrorCS", {"start": v(-76.75, 5) * mm, "end": v(-68.25, 5) * mm});
            skLineSegment(sketch, "E41.MirrorCS", {"start": v(-68.25, -5) * mm, "end": v(-68.25, 5) * mm});
            skLineSegment(sketch, "E42.MirrorCS", {"start": v(-76.75, -5) * mm, "end": v(-76.75, 5) * mm});
            skSolve(sketch);
        }
        {
            var Q0;
            {var subQ0=sQuery(id+"F14.wireOp",EDGE,"E33.bottom");Q0=makeQuery(id+"F14.imprint","IMPRINT",FACE,{"disambiguationData":[TD([[makeQuery(id+"F14.imprint","IMPRINT",EDGE,{"derivedFrom":subQ0}),-1.0]])]});}
            var Q1;
            {var subQ0=sQuery(id+"F14.wireOp",EDGE,"E33.top");Q1=makeQuery(id+"F14.imprint","IMPRINT",FACE,{"disambiguationData":[TD([[makeQuery(id+"F14.imprint","IMPRINT",EDGE,{"derivedFrom":subQ0}),1.0]])]});}
            var Q2;
            {var subQ0=sQuery(id+"F14.wireOp",EDGE,"E35.MirrorCS");Q2=makeQuery(id+"F14.imprint","IMPRINT",FACE,{"disambiguationData":[TD([[makeQuery(id+"F14.imprint","IMPRINT",EDGE,{"derivedFrom":subQ0}),1.0]])]});}
            var Q3;
            {var subQ0=sQuery(id+"F14.wireOp",EDGE,"E37.MirrorCS");Q3=makeQuery(id+"F14.imprint","IMPRINT",FACE,{"disambiguationData":[TD([[makeQuery(id+"F14.imprint","IMPRINT",EDGE,{"derivedFrom":subQ0}),-1.0]])]});}
            extrude(context, id + "F15", {"entities" : qUnion([Q0, Q1, Q2, Q3]), "operationType" : NewBodyOperationType.REMOVE, "endBound" : BoundingType.THROUGH_ALL, "depth" : 25 * mm, "offsetDistance" : 25 * mm, "hasSecondDirection" : true, "secondDirectionBound" : SecondDirectionBoundingType.THROUGH_ALL, "secondDirectionOppositeDirection" : true, "secondDirectionDepth" : 25 * mm});
        }
        {
            var Q0;
            Q0=makeQuery(id+"F7.boolean.opBoolean","COPY",EDGE,{"derivedFrom":makeQuery(id+"F7.opExtrude","SWEPT_EDGE",EDGE,{"disambiguationData":[OSD([sQuery(id+"F6.wireOp",EDGE,"E17"),sQuery(id+"F6.wireOp",EDGE,"E23.MirrorCS")])]})});
            var Q1;
            Q1=makeQuery(id+"F7.boolean.opBoolean","COPY",EDGE,{"derivedFrom":makeQuery(id+"F7.opExtrude","SWEPT_EDGE",EDGE,{"disambiguationData":[OSD([sQuery(id+"F6.wireOp",EDGE,"E14.5"),sQuery(id+"F6.wireOp",EDGE,"E22.MirrorCS")])]})});
            var Q2;
            Q2=makeQuery(id+"F7.boolean.opBoolean","COPY",EDGE,{"derivedFrom":makeQuery(id+"F7.opExtrude","SWEPT_EDGE",EDGE,{"disambiguationData":[OSD([sQuery(id+"F6.wireOp",EDGE,"E17"),sQuery(id+"F6.wireOp",EDGE,"E19"),sQuery(id+"F6.wireOp",EDGE,"E21")])]})});
            var Q3;
            Q3=makeQuery(id+"F7.boolean.opBoolean","COPY",EDGE,{"derivedFrom":makeQuery(id+"F7.opExtrude","SWEPT_EDGE",EDGE,{"disambiguationData":[OSD([sQuery(id+"F6.wireOp",EDGE,"E19"),sQuery(id+"F6.wireOp",EDGE,"E23.MirrorCS")])]})});
            var Q4;
            Q4=makeQuery(id+"F7.boolean.opBoolean","COPY",EDGE,{"derivedFrom":makeQuery(id+"F7.opExtrude","SWEPT_EDGE",EDGE,{"disambiguationData":[OSD([sQuery(id+"F6.wireOp",EDGE,"E14.0"),sQuery(id+"F6.wireOp",EDGE,"E23.MirrorCS")])]})});
            var Q5;
            Q5=makeQuery(id+"F7.boolean.opBoolean","COPY",EDGE,{"derivedFrom":makeQuery(id+"F7.opExtrude","SWEPT_EDGE",EDGE,{"disambiguationData":[OSD([sQuery(id+"F6.wireOp",EDGE,"E18"),sQuery(id+"F6.wireOp",EDGE,"E23.MirrorCS")])]})});
            var Q6;
            Q6=makeQuery(id+"F7.boolean.opBoolean","COPY",EDGE,{"derivedFrom":makeQuery(id+"F7.opExtrude","SWEPT_EDGE",EDGE,{"disambiguationData":[OSD([sQuery(id+"F6.wireOp",EDGE,"E14.0"),sQuery(id+"F6.wireOp",EDGE,"E18"),sQuery(id+"F6.wireOp",EDGE,"E20")])]})});
            var Q7;
            Q7=makeQuery(id+"F7.boolean.opBoolean","COPY",EDGE,{"derivedFrom":makeQuery(id+"F7.opExtrude","SWEPT_EDGE",EDGE,{"disambiguationData":[OSD([sQuery(id+"F6.wireOp",EDGE,"E16"),sQuery(id+"F6.wireOp",EDGE,"E22.MirrorCS")])]})});
            var Q8;
            Q8=makeQuery(id+"F7.boolean.opBoolean","COPY",EDGE,{"derivedFrom":makeQuery(id+"F7.opExtrude","SWEPT_EDGE",EDGE,{"disambiguationData":[OSD([sQuery(id+"F6.wireOp",EDGE,"E19"),sQuery(id+"F6.wireOp",EDGE,"E22.MirrorCS")])]})});
            var Q9;
            Q9=makeQuery(id+"F7.boolean.opBoolean","COPY",EDGE,{"derivedFrom":makeQuery(id+"F7.opExtrude","SWEPT_EDGE",EDGE,{"disambiguationData":[OSD([sQuery(id+"F6.wireOp",EDGE,"E16"),sQuery(id+"F6.wireOp",EDGE,"E18")])]})});
            var Q10;
            Q10=makeQuery(id+"F7.boolean.opBoolean","COPY",EDGE,{"derivedFrom":makeQuery(id+"F7.opExtrude","SWEPT_EDGE",EDGE,{"disambiguationData":[OSD([sQuery(id+"F6.wireOp",EDGE,"E14.5"),sQuery(id+"F6.wireOp",EDGE,"E19")])]})});
            var Q11;
            Q11=makeQuery(id+"F7.boolean.opBoolean","COPY",EDGE,{"derivedFrom":makeQuery(id+"F7.opExtrude","SWEPT_EDGE",EDGE,{"disambiguationData":[OSD([sQuery(id+"F6.wireOp",EDGE,"E18"),sQuery(id+"F6.wireOp",EDGE,"E22.MirrorCS")])]})});
            fillet(context, id + "F16", {"entities" : qUnion([Q0, Q1, Q2, Q3, Q4, Q5, Q6, Q7, Q8, Q9, Q10, Q11]), "radius" : 2.5 * mm, "tangentPropagation" : true, "allowEdgeOverflow" : false});
        }
        {
            var Q0;
            Q0=makeQuery(id+"F15.boolean.opBoolean","COPY",EDGE,{"derivedFrom":makeQuery(id+"F15.opExtrude","SWEPT_EDGE",EDGE,{"disambiguationData":[OSD([sQuery(id+"F14.wireOp",EDGE,"E33.bottom"),sQuery(id+"F14.wireOp",EDGE,"E33.right")])]})});
            var Q1;
            Q1=makeQuery(id+"F15.boolean.opBoolean","COPY",EDGE,{"derivedFrom":makeQuery(id+"F15.opExtrude","SWEPT_EDGE",EDGE,{"disambiguationData":[OSD([sQuery(id+"F14.wireOp",EDGE,"E33.bottom"),sQuery(id+"F14.wireOp",EDGE,"E33.left")])]})});
            var Q2;
            Q2=makeQuery(id+"F15.boolean.opBoolean","COPY",EDGE,{"derivedFrom":makeQuery(id+"F15.opExtrude","SWEPT_EDGE",EDGE,{"disambiguationData":[OSD([sQuery(id+"F14.wireOp",EDGE,"E33.right"),sQuery(id+"F14.wireOp",EDGE,"E38.bottom"),sQuery(id+"F14.wireOp",EDGE,"E38.right")])]})});
            var Q3;
            Q3=makeQuery(id+"F15.boolean.opBoolean","COPY",EDGE,{"derivedFrom":makeQuery(id+"F15.opExtrude","SWEPT_EDGE",EDGE,{"disambiguationData":[OSD([sQuery(id+"F14.wireOp",EDGE,"E33.left"),sQuery(id+"F14.wireOp",EDGE,"E38.bottom"),sQuery(id+"F14.wireOp",EDGE,"E38.left")])]})});
            var Q4;
            Q4=makeQuery(id+"F15.boolean.opBoolean","COPY",EDGE,{"derivedFrom":makeQuery(id+"F15.opExtrude","SWEPT_EDGE",EDGE,{"disambiguationData":[OSD([sQuery(id+"F14.wireOp",EDGE,"E33.top"),sQuery(id+"F14.wireOp",EDGE,"E33.left")])]})});
            var Q5;
            Q5=makeQuery(id+"F15.boolean.opBoolean","COPY",EDGE,{"derivedFrom":makeQuery(id+"F15.opExtrude","SWEPT_EDGE",EDGE,{"disambiguationData":[OSD([sQuery(id+"F14.wireOp",EDGE,"E33.top"),sQuery(id+"F14.wireOp",EDGE,"E33.right")])]})});
            var Q6;
            Q6=makeQuery(id+"F15.boolean.opBoolean","COPY",EDGE,{"derivedFrom":makeQuery(id+"F15.opExtrude","SWEPT_EDGE",EDGE,{"disambiguationData":[OSD([sQuery(id+"F14.wireOp",EDGE,"E33.right"),sQuery(id+"F14.wireOp",EDGE,"E38.top"),sQuery(id+"F14.wireOp",EDGE,"E38.right")])]})});
            var Q7;
            Q7=makeQuery(id+"F15.boolean.opBoolean","COPY",EDGE,{"derivedFrom":makeQuery(id+"F15.opExtrude","SWEPT_EDGE",EDGE,{"disambiguationData":[OSD([sQuery(id+"F14.wireOp",EDGE,"E33.left"),sQuery(id+"F14.wireOp",EDGE,"E38.top"),sQuery(id+"F14.wireOp",EDGE,"E38.left")])]})});
            var Q8;
            Q8=makeQuery(id+"F15.boolean.opBoolean","COPY",EDGE,{"derivedFrom":makeQuery(id+"F15.opExtrude","SWEPT_EDGE",EDGE,{"disambiguationData":[OSD([sQuery(id+"F14.wireOp",EDGE,"E34.MirrorCS"),sQuery(id+"F14.wireOp",EDGE,"E40.MirrorCS"),sQuery(id+"F14.wireOp",EDGE,"E42.MirrorCS")])]})});
            var Q9;
            Q9=makeQuery(id+"F15.boolean.opBoolean","COPY",EDGE,{"derivedFrom":makeQuery(id+"F15.opExtrude","SWEPT_EDGE",EDGE,{"disambiguationData":[OSD([sQuery(id+"F14.wireOp",EDGE,"E36.MirrorCS"),sQuery(id+"F14.wireOp",EDGE,"E40.MirrorCS"),sQuery(id+"F14.wireOp",EDGE,"E41.MirrorCS")])]})});
            var Q10;
            Q10=makeQuery(id+"F15.boolean.opBoolean","COPY",EDGE,{"derivedFrom":makeQuery(id+"F15.opExtrude","SWEPT_EDGE",EDGE,{"disambiguationData":[OSD([sQuery(id+"F14.wireOp",EDGE,"E34.MirrorCS"),sQuery(id+"F14.wireOp",EDGE,"E37.MirrorCS")])]})});
            var Q11;
            Q11=makeQuery(id+"F15.boolean.opBoolean","COPY",EDGE,{"derivedFrom":makeQuery(id+"F15.opExtrude","SWEPT_EDGE",EDGE,{"disambiguationData":[OSD([sQuery(id+"F14.wireOp",EDGE,"E36.MirrorCS"),sQuery(id+"F14.wireOp",EDGE,"E37.MirrorCS")])]})});
            var Q12;
            Q12=makeQuery(id+"F15.boolean.opBoolean","COPY",EDGE,{"derivedFrom":makeQuery(id+"F15.opExtrude","SWEPT_EDGE",EDGE,{"disambiguationData":[OSD([sQuery(id+"F14.wireOp",EDGE,"E34.MirrorCS"),sQuery(id+"F14.wireOp",EDGE,"E39.MirrorCS"),sQuery(id+"F14.wireOp",EDGE,"E42.MirrorCS")])]})});
            var Q13;
            Q13=makeQuery(id+"F15.boolean.opBoolean","COPY",EDGE,{"derivedFrom":makeQuery(id+"F15.opExtrude","SWEPT_EDGE",EDGE,{"disambiguationData":[OSD([sQuery(id+"F14.wireOp",EDGE,"E36.MirrorCS"),sQuery(id+"F14.wireOp",EDGE,"E39.MirrorCS"),sQuery(id+"F14.wireOp",EDGE,"E41.MirrorCS")])]})});
            var Q14;
            Q14=makeQuery(id+"F15.boolean.opBoolean","COPY",EDGE,{"derivedFrom":makeQuery(id+"F15.opExtrude","SWEPT_EDGE",EDGE,{"disambiguationData":[OSD([sQuery(id+"F14.wireOp",EDGE,"E35.MirrorCS"),sQuery(id+"F14.wireOp",EDGE,"E36.MirrorCS")])]})});
            var Q15;
            Q15=makeQuery(id+"F15.boolean.opBoolean","COPY",EDGE,{"derivedFrom":makeQuery(id+"F15.opExtrude","SWEPT_EDGE",EDGE,{"disambiguationData":[OSD([sQuery(id+"F14.wireOp",EDGE,"E34.MirrorCS"),sQuery(id+"F14.wireOp",EDGE,"E35.MirrorCS")])]})});
            fillet(context, id + "F17", {"entities" : qUnion([Q0, Q1, Q2, Q3, Q4, Q5, Q6, Q7, Q8, Q9, Q10, Q11, Q12, Q13, Q14, Q15]), "radius" : (8.5 / 2) * mm, "tangentPropagation" : true, "allowEdgeOverflow" : false});
        }
        {
            var Q0;
            {var subQ0=sQuery(id+"F8.wireOp",EDGE,"E28.trimOffspring");var subQ1=sQuery(id+"F8.wireOp",EDGE,"E27.trimOffspring");var subQ2=sQuery(id+"F8.wireOp",EDGE,"E24.right");var subQ3=sQuery(id+"F8.wireOp",EDGE,"E24.left");var subQ4=sQuery(id+"F8.wireOp",EDGE,"E24.top");var subQ5=sQuery(id+"F8.wireOp",EDGE,"E24.bottom");Q0=makeQuery(id+"F11.boolean.opBoolean","MERGE",FACE,{"derivedFrom":[makeQuery(id+"F9.boolean.opBoolean","MERGE",FACE,{"derivedFrom":[makeQuery(id+"F1.opExtrude","CAP_FACE",FACE,{"disambiguationData":[OSD([sQuery(id+"F0.wireOp",EDGE,"E0.bottom"),sQuery(id+"F0.wireOp",EDGE,"E0.top"),sQuery(id+"F0.wireOp",EDGE,"E0.left"),sQuery(id+"F0.wireOp",EDGE,"E0.right")])],"isStart":true}),makeQuery(id+"F9.opExtrude","CAP_FACE",FACE,{"disambiguationData":[OSD([subQ5,subQ4,subQ3,sQuery(id+"F8.wireOp",EDGE,"E29.bottom"),sQuery(id+"F8.wireOp",EDGE,"E29.top"),sQuery(id+"F8.wireOp",EDGE,"E29.right")])],"isStart":true}),makeQuery(id+"F9.opExtrude","CAP_FACE",FACE,{"disambiguationData":[OSD([subQ2,subQ1,subQ0,sQuery(id+"F8.wireOp",EDGE,"E30.bottom"),sQuery(id+"F8.wireOp",EDGE,"E30.top"),sQuery(id+"F8.wireOp",EDGE,"E30.right")])],"isStart":true})]}),makeQuery(id+"F11.opExtrude","CAP_FACE",FACE,{"disambiguationData":[OSD([subQ5,subQ4,subQ3,sQuery(id+"F8.wireOp",EDGE,"E25")])],"isStart":true}),makeQuery(id+"F11.opExtrude","CAP_FACE",FACE,{"disambiguationData":[OSD([subQ2,subQ1,subQ0,sQuery(id+"F8.wireOp",EDGE,"E26")])],"isStart":true})]});}
            var sketch = newSketch(context, id + "F18", { "sketchPlane" : qUnion([Q0])});
            skLineSegment(sketch, "E43.bottom", {"start": v(-57.5, -43.5) * mm, "end": v(57.5, -43.5) * mm});
            skLineSegment(sketch, "E43.top", {"start": v(-57.5, -38.5) * mm, "end": v(57.5, -38.5) * mm});
            skLineSegment(sketch, "E43.left", {"start": v(-57.5, -43.5) * mm, "end": v(-57.5, -38.5) * mm});
            skLineSegment(sketch, "E43.right", {"start": v(57.5, -43.5) * mm, "end": v(57.5, -38.5) * mm});
            skLineSegment(sketch, "E44.bottom", {"start": v(-57.5, 38.5) * mm, "end": v(57.5, 38.5) * mm});
            skLineSegment(sketch, "E44.top", {"start": v(-57.5, 43.5) * mm, "end": v(57.5, 43.5) * mm});
            skLineSegment(sketch, "E44.left", {"start": v(-57.5, 38.5) * mm, "end": v(-57.5, 43.5) * mm});
            skLineSegment(sketch, "E44.right", {"start": v(57.5, 38.5) * mm, "end": v(57.5, 43.5) * mm});
            skSolve(sketch);
        }
        {
            var Q0;
            Q0=makeQuery(id+"F18.imprint","IMPRINT",FACE,{"disambiguationData":[TD([[makeQuery(id+"F18.imprint","IMPRINT",EDGE,{"derivedFrom":sQuery(id+"F18.wireOp",EDGE,"E44.top")}),-1.0]])]});
            var Q1;
            Q1=makeQuery(id+"F18.imprint","IMPRINT",FACE,{"disambiguationData":[TD([[makeQuery(id+"F18.imprint","IMPRINT",EDGE,{"derivedFrom":sQuery(id+"F18.wireOp",EDGE,"E43.bottom")}),1.0]])]});
            var Q2;
            {var subQ0=sQuery(id+"F4.wireOp",EDGE,"E13");var subQ1=sQuery(id+"F4.wireOp",EDGE,"E12");var subQ2=sQuery(id+"F4.wireOp",EDGE,"E9.MirrorCS");var subQ3=sQuery(id+"F4.wireOp",EDGE,"E8.MirrorCS");var subQ4=sQuery(id+"F4.wireOp",EDGE,"E5.MirrorCS");var subQ5=sQuery(id+"F4.wireOp",EDGE,"E4.1.0.2");var subQ6=sQuery(id+"F4.wireOp",EDGE,"E3.right");var subQ7=sQuery(id+"F4.wireOp",EDGE,"E3.top");var subQ8=sQuery(id+"F0.wireOp",EDGE,"E0.right");var subQ9=sQuery(id+"F0.wireOp",EDGE,"E0.left");var subQ10=sQuery(id+"F0.wireOp",EDGE,"E0.top");var subQ11=sQuery(id+"F0.wireOp",EDGE,"E0.bottom");Q2=makeQuery(id+"F13.boolean.opBoolean","MERGE",FACE,{"derivedFrom":[makeQuery(id+"F5.opExtrude","CAP_FACE",FACE,{"disambiguationData":[OSD([subQ11,subQ10,subQ9,subQ8,subQ7,subQ6,subQ5,subQ4,subQ3,subQ2,subQ1,subQ0])],"isStart":false}),makeQuery(id+"F11.opExtrude","CAP_FACE",FACE,{"disambiguationData":[OSD([sQuery(id+"F8.wireOp",EDGE,"E24.bottom"),sQuery(id+"F8.wireOp",EDGE,"E24.top"),sQuery(id+"F8.wireOp",EDGE,"E24.left"),sQuery(id+"F8.wireOp",EDGE,"E25")])],"isStart":false}),makeQuery(id+"F11.opExtrude","CAP_FACE",FACE,{"disambiguationData":[OSD([sQuery(id+"F8.wireOp",EDGE,"E24.right"),sQuery(id+"F8.wireOp",EDGE,"E27.trimOffspring"),sQuery(id+"F8.wireOp",EDGE,"E28.trimOffspring"),sQuery(id+"F8.wireOp",EDGE,"E26")])],"isStart":false}),makeQuery(id+"F13.opExtrude","CAP_FACE",FACE,{"disambiguationData":[OSD([subQ11,subQ10,subQ9,subQ8,subQ7,subQ6,sQuery(id+"F4.wireOp",EDGE,"E4.1.0.1"),subQ5,subQ4,subQ3,subQ2,sQuery(id+"F4.wireOp",EDGE,"E10.MirrorCS"),subQ1,subQ0,sQuery(id+"F12.wireOp",EDGE,"E31.bottom"),sQuery(id+"F12.wireOp",EDGE,"E31.top"),sQuery(id+"F12.wireOp",EDGE,"E31.right")])],"isStart":true}),makeQuery(id+"F13.opExtrude","CAP_FACE",FACE,{"disambiguationData":[OSD([subQ11,subQ10,subQ9,subQ8,subQ7,sQuery(id+"F4.wireOp",EDGE,"E3.left"),subQ6,subQ5,subQ4,sQuery(id+"F4.wireOp",EDGE,"E6.MirrorCS"),subQ3,subQ2,subQ1,subQ0,sQuery(id+"F12.wireOp",EDGE,"E32.bottom"),sQuery(id+"F12.wireOp",EDGE,"E32.top"),sQuery(id+"F12.wireOp",EDGE,"E32.right")])],"isStart":true})]});}
            extrude(context, id + "F19", {"entities" : qUnion([Q0, Q1]), "operationType" : NewBodyOperationType.ADD, "endBound" : BoundingType.UP_TO_SURFACE, "oppositeDirection" : true, "depth" : 25 * mm, "endBoundEntityFace" : qUnion([Q2]), "offsetDistance" : 25 * mm});
        }
        {
            var Q0;
            Q0=makeQuery(id+"F11.opExtrude","SWEPT_EDGE",EDGE,{"disambiguationData":[OSD([sQuery(id+"F8.wireOp",EDGE,"E24.top"),sQuery(id+"F8.wireOp",EDGE,"E24.left")])]});
            var Q1;
            Q1=makeQuery(id+"F11.opExtrude","SWEPT_EDGE",EDGE,{"disambiguationData":[OSD([sQuery(id+"F8.wireOp",EDGE,"E24.bottom"),sQuery(id+"F8.wireOp",EDGE,"E24.left")])]});
            var Q2;
            Q2=makeQuery(id+"F11.opExtrude","SWEPT_EDGE",EDGE,{"disambiguationData":[OSD([sQuery(id+"F8.wireOp",EDGE,"E24.bottom"),sQuery(id+"F8.wireOp",EDGE,"E25")])]});
            var Q3;
            Q3=makeQuery(id+"F11.opExtrude","SWEPT_EDGE",EDGE,{"disambiguationData":[OSD([sQuery(id+"F8.wireOp",EDGE,"E24.top"),sQuery(id+"F8.wireOp",EDGE,"E25")])]});
            var Q4;
            Q4=makeQuery(id+"F13.opExtrude","SWEPT_EDGE",EDGE,{"disambiguationData":[OSD([sQuery(id+"F12.wireOp",EDGE,"E31.top"),sQuery(id+"F12.wireOp",EDGE,"E31.right")])]});
            var Q5;
            Q5=makeQuery(id+"F13.opExtrude","SWEPT_EDGE",EDGE,{"disambiguationData":[OSD([sQuery(id+"F12.wireOp",EDGE,"E31.bottom"),sQuery(id+"F12.wireOp",EDGE,"E31.right")])]});
            var Q6;
            Q6=makeQuery(id+"F13.opExtrude","SWEPT_EDGE",EDGE,{"disambiguationData":[OSD([sQuery(id+"F12.wireOp",EDGE,"E32.bottom"),sQuery(id+"F12.wireOp",EDGE,"E32.right")])]});
            var Q7;
            Q7=makeQuery(id+"F11.opExtrude","SWEPT_EDGE",EDGE,{"disambiguationData":[OSD([sQuery(id+"F8.wireOp",EDGE,"E24.top"),sQuery(id+"F8.wireOp",EDGE,"E26")])]});
            var Q8;
            Q8=makeQuery(id+"F11.opExtrude","SWEPT_EDGE",EDGE,{"disambiguationData":[OSD([sQuery(id+"F8.wireOp",EDGE,"E24.top"),sQuery(id+"F8.wireOp",EDGE,"E24.right")])]});
            var Q9;
            Q9=makeQuery(id+"F11.opExtrude","SWEPT_EDGE",EDGE,{"disambiguationData":[OSD([sQuery(id+"F8.wireOp",EDGE,"E24.bottom"),sQuery(id+"F8.wireOp",EDGE,"E24.right")])]});
            var Q10;
            Q10=makeQuery(id+"F11.opExtrude","SWEPT_EDGE",EDGE,{"disambiguationData":[OSD([sQuery(id+"F8.wireOp",EDGE,"E24.bottom"),sQuery(id+"F8.wireOp",EDGE,"E26")])]});
            var Q11;
            Q11=makeQuery(id+"F13.opExtrude","SWEPT_EDGE",EDGE,{"disambiguationData":[OSD([sQuery(id+"F12.wireOp",EDGE,"E32.top"),sQuery(id+"F12.wireOp",EDGE,"E32.right")])]});
            var Q12;
            {var subQ0=sQuery(id+"F4.wireOp",EDGE,"E13");Q12=makeQuery(id+"F10.opFillet","BLEND_EDGE",EDGE,{"blendedFrom":[makeQuery(id+"F5.opExtrude","SWEPT_EDGE",EDGE,{"disambiguationData":[OSD([sQuery(id+"F0.wireOp",EDGE,"E0.top"),sQuery(id+"F4.wireOp",EDGE,"E11.MirrorCS"),subQ0])]}),makeQuery(id+"F5.opExtrude","SWEPT_FACE",FACE,{"disambiguationData":[OSD([subQ0])]})],"blendedInto":[makeQuery(id+"F5.opExtrude","SWEPT_FACE",FACE,{"disambiguationData":[OSD([subQ0])]})]});}
            var Q13;
            {var subQ0=sQuery(id+"F4.wireOp",EDGE,"E12");Q13=makeQuery(id+"F10.opFillet","BLEND_EDGE",EDGE,{"blendedFrom":[makeQuery(id+"F5.opExtrude","SWEPT_EDGE",EDGE,{"disambiguationData":[OSD([sQuery(id+"F0.wireOp",EDGE,"E0.bottom"),sQuery(id+"F4.wireOp",EDGE,"E4.1.0.0"),subQ0])]}),makeQuery(id+"F5.opExtrude","SWEPT_FACE",FACE,{"disambiguationData":[OSD([subQ0])]})],"blendedInto":[makeQuery(id+"F5.opExtrude","SWEPT_FACE",FACE,{"disambiguationData":[OSD([subQ0])]})]});}
            var Q14;
            Q14=makeQuery(id+"F19.opExtrude","SWEPT_EDGE",EDGE,{"disambiguationData":[OSD([sQuery(id+"F18.wireOp",EDGE,"E43.top"),sQuery(id+"F18.wireOp",EDGE,"E43.right")])]});
            var Q15;
            Q15=makeQuery(id+"F19.opExtrude","SWEPT_EDGE",EDGE,{"disambiguationData":[OSD([sQuery(id+"F18.wireOp",EDGE,"E44.bottom"),sQuery(id+"F18.wireOp",EDGE,"E44.right")])]});
            var Q16;
            {var subQ0=sQuery(id+"F4.wireOp",EDGE,"E3.right");Q16=makeQuery(id+"F10.opFillet","BLEND_EDGE",EDGE,{"blendedFrom":[makeQuery(id+"F5.opExtrude","SWEPT_EDGE",EDGE,{"disambiguationData":[OSD([sQuery(id+"F0.wireOp",EDGE,"E0.bottom"),sQuery(id+"F4.wireOp",EDGE,"E3.bottom"),subQ0])]}),makeQuery(id+"F5.opExtrude","SWEPT_FACE",FACE,{"disambiguationData":[OSD([subQ0])]})],"blendedInto":[makeQuery(id+"F5.opExtrude","SWEPT_FACE",FACE,{"disambiguationData":[OSD([subQ0])]})]});}
            var Q17;
            Q17=makeQuery(id+"F19.opExtrude","SWEPT_EDGE",EDGE,{"disambiguationData":[OSD([sQuery(id+"F18.wireOp",EDGE,"E43.top"),sQuery(id+"F18.wireOp",EDGE,"E43.left")])]});
            var Q18;
            Q18=makeQuery(id+"F19.opExtrude","SWEPT_EDGE",EDGE,{"disambiguationData":[OSD([sQuery(id+"F18.wireOp",EDGE,"E44.bottom"),sQuery(id+"F18.wireOp",EDGE,"E44.left")])]});
            var Q19;
            {var subQ0=sQuery(id+"F4.wireOp",EDGE,"E8.MirrorCS");Q19=makeQuery(id+"F10.opFillet","BLEND_EDGE",EDGE,{"blendedFrom":[makeQuery(id+"F5.opExtrude","SWEPT_EDGE",EDGE,{"disambiguationData":[OSD([sQuery(id+"F0.wireOp",EDGE,"E0.top"),subQ0])]}),makeQuery(id+"F5.opExtrude","SWEPT_FACE",FACE,{"disambiguationData":[OSD([subQ0])]})],"blendedInto":[makeQuery(id+"F5.opExtrude","SWEPT_FACE",FACE,{"disambiguationData":[OSD([subQ0])]})]});}
            fillet(context, id + "F20", {"entities" : qUnion([Q0, Q1, Q2, Q3, Q4, Q5, Q6, Q7, Q8, Q9, Q10, Q11, Q12, Q13, Q14, Q15, Q16, Q17, Q18, Q19]), "radius" : 5 * mm, "tangentPropagation" : true, "allowEdgeOverflow" : false});
        }
    });
